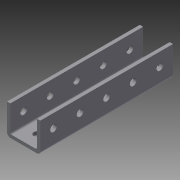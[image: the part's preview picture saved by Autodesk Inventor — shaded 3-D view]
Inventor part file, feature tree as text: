
AUTODESK INVENTOR PART (.ipt)
format: ipt  version: 2014 (Build 180170000, 170)  size: 120,320 bytes
history: native  units: in
note: dims shown in document units (in); Inventor stores cm internally (conversion verified against a paired STEP export)
features: sketch x3, hole x2, extrude x1, pattern_linear x1
ambient origin geometry x8: Origin, YZ Plane, XZ Plane, XY Plane, X Axis, Y Axis, Z Axis, Center Point
bodies: Solid1 (feature_tree)
feature tree (7):
  extrude  "Extrusion1"  Depth=5.0in TaperAngle=0.0deg
  sketch  "Sketch2"  dims[d6=0.5in d7=0.5in]
  sketch  "Sketch3"  dims[d8=0.25in d9=0.75in d10=0.375in d11=0.25in d12=0.5635in d13=1.0in d14=0.8108in d15=0.25in d16=0.75in d17=0.375in d18=0.25in d19=0.5635in d20=1.0in d21=0.8108in d22=1.9685in d24=1.0in]
  hole  "Hole1"  [1 undecoded]
  hole  "Hole2"  [1 undecoded]
  pattern_linear  "Rectangular Pattern1"  [2 undecoded]
  sketch  "Sketch1"  dims[d0=1.25in d1=1.125in d2=0.0625in d3=0.125in d4=5.0in d5=0.0in]
note: 4 required parameter values undecoded (feature->parameter linkage not recoverable at this tier; creation-order binding heuristic only, values carry confidence <= 0.55)
